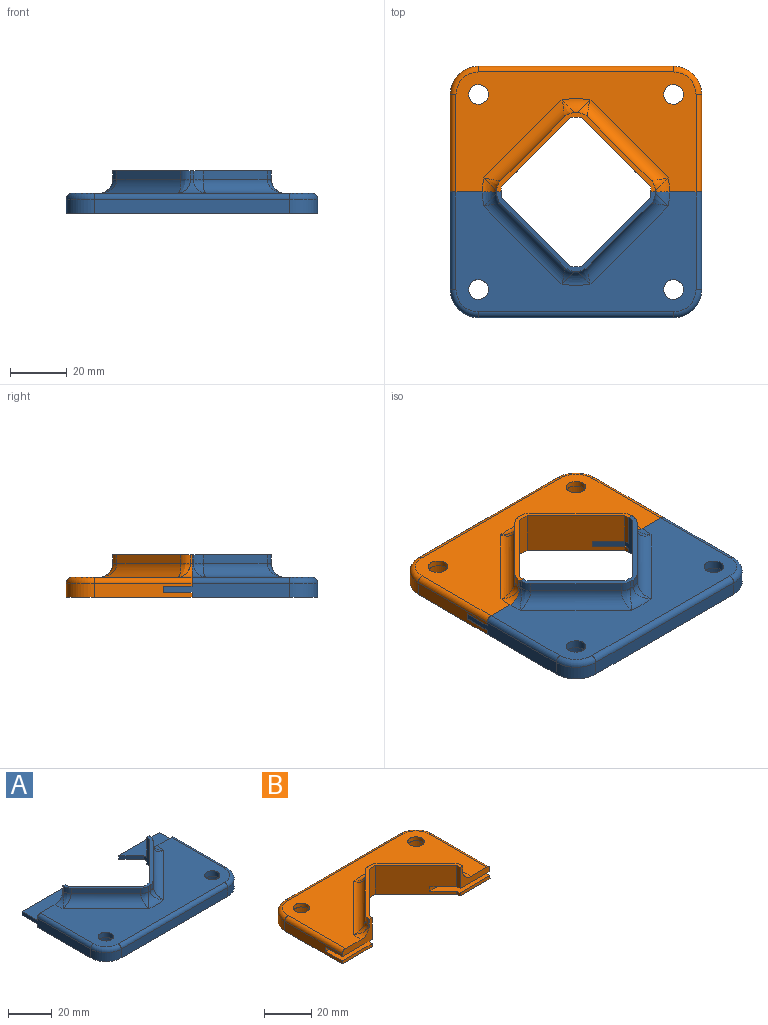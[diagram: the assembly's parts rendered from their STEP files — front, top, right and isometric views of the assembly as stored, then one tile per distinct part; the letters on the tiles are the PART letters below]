
ASSEMBLY  parts=2 mates=1
PART A: 54 faces, bbox 90.5x55.3x15.6 mm
  f0: plane 44.5x5mm, normal (1,0,0), area 192.5mm2, adj f2,f9,f35,f44,f45,f46,f47,f48
  f1: plane 44.5x5mm, normal (-1,0,0), area 192.5mm2, adj f2,f7,f31,f49,f50,f51,f52,f53
  f2: plane 88.9x44.45mm, normal (0,0,-1), area 2850.6mm2, adj f0,f1,f3,f4,f5,f6,f7,f8
  f3: cylinder r=26.44mm len=15mm, axis (0,0,-1), area 32.6mm2, adj f2,f20,f21,f25,f50,f51,f52,f53
  f4: cylinder r=26.44mm len=15mm, axis (0,0,-1), area 32.6mm2, adj f2,f22,f23,f25,f44,f45,f46,f47
  f5: cylinder r=6.5mm len=13mm, axis (0,0,-1), area 163.4mm2, adj f2,f14
  f6: cylinder r=6.5mm len=13mm, axis (0,0,-1), area 163.4mm2, adj f2,f12
  f7: cylinder r=9.95mm len=9.95mm, axis (0,0,-1), area 78.1mm2, adj f1,f2,f8,f32
  f8: plane 69x5mm, normal (0,-1,0), area 345mm2, adj f2,f7,f9,f33
  f9: cylinder r=9.95mm len=9.95mm, axis (0,0,-1), area 78.1mm2, adj f0,f2,f8,f34
  f10: plane 84.9x42.45mm, normal (0,0,1), area 2128.9mm2, adj f11,f13,f26,f27,f28,f29,f30,f31
  f11: cylinder r=3.5mm len=7mm, axis (0,0,-1), area 66mm2, adj f10,f12
  f12: plane 13x13mm, normal (0,0,-1), area 94.2mm2, adj f6,f11
  f13: cylinder r=3.5mm len=7mm, axis (0,0,-1), area 66mm2, adj f10,f14
  f14: plane 13x13mm, normal (0,0,-1), area 94.2mm2, adj f5,f13
  f15: plane 22.6x22.6mm, normal (0.71,-0.71,0), area 95.9mm2, adj f25,f27,f37,f41
  f16: cylinder r=28.04mm len=3mm, axis (0,0,-1), area 1.6mm2, adj f25,f29,f41,f46
  f17: cylinder r=28.04mm len=3mm, axis (0,0,-1), area 1.6mm2, adj f25,f30,f43,f51
  f18: plane 22.6x22.6mm, normal (-0.71,-0.71,0), area 95.9mm2, adj f25,f28,f39,f43
  f19: cylinder r=26.44mm len=15mm, axis (0,0,-1), area 57.5mm2, adj f2,f20,f23,f25
  f20: plane 24.46x24.46mm, normal (0.71,0.71,0), area 518.8mm2, adj f2,f3,f19,f25
  f21: plane 8.09x8.09mm, normal (0.71,-0.71,0), area 22.9mm2, adj f3,f49,f52,f53
  f22: plane 8.09x8.09mm, normal (-0.71,-0.71,0), area 22.9mm2, adj f4,f44,f47,f48
  f23: plane 24.46x24.46mm, normal (-0.71,0.71,0), area 518.8mm2, adj f2,f4,f19,f25
  f24: cylinder r=28.04mm len=3mm, axis (0,0,-1), area 3.2mm2, adj f25,f26,f37,f39
  f25: plane 56.08x28.04mm, normal (0,0,1), area 125.3mm2, adj f3,f4,f15,f16,f17,f18,f19,f20
  f26: torus R=33.04mm, axis (0,0,1), area 34.8mm2, adj f10,f24,f36,f38
  f27: cylinder r=5mm len=31.25mm, axis (0.71,0.71,0), area 272.4mm2, adj f10,f15,f36,f40
  f28: cylinder r=5mm len=31.25mm, axis (0.71,-0.71,0), area 272.4mm2, adj f10,f18,f38,f42
  f29: torus R=33.04mm, axis (0,0,1), area 17.4mm2, adj f10,f16,f40,f46
  f30: torus R=33.04mm, axis (0,0,1), area 17.4mm2, adj f10,f17,f42,f51
  f31: cylinder r=2mm len=34.5mm, axis (0,1,0), area 108.4mm2, adj f1,f10,f32,f51
  f32: torus R=7.95mm, axis (0,0,1), area 45.5mm2, adj f7,f10,f31,f33
  f33: cylinder r=2mm len=69mm, axis (-1,0,0), area 216.8mm2, adj f8,f10,f32,f34
  f34: torus R=7.95mm, axis (0,0,1), area 45.5mm2, adj f9,f10,f33,f35
  f35: cylinder r=2mm len=34.5mm, axis (0,-1,0), area 108.4mm2, adj f0,f10,f34,f46
  f36: bspline ~6.1x5.89mm, area 18.9mm2, adj f26,f27,f37
  f37: cylinder r=5mm len=3.44mm, axis (0,0,-1), area 11.5mm2, adj f15,f24,f25,f36
  f38: bspline ~6.1x5.89mm, area 18.9mm2, adj f26,f28,f39
  f39: cylinder r=5mm len=3.44mm, axis (0,0,-1), area 11.5mm2, adj f18,f24,f25,f38
  f40: bspline ~6.1x5.89mm, area 18.9mm2, adj f27,f29,f41
  f41: cylinder r=5mm len=3.44mm, axis (0,0,-1), area 11.5mm2, adj f15,f16,f25,f40
  f42: bspline ~6.1x5.89mm, area 18.9mm2, adj f28,f30,f43
  f43: cylinder r=5mm len=3.44mm, axis (0,0,-1), area 11.5mm2, adj f17,f18,f25,f42
  f44: plane 26.17x10mm, normal (0,0,-1), area 213.4mm2, adj f0,f4,f22,f45,f48
  f45: plane 18.01x1.8mm, normal (0,1,0), area 32.4mm2, adj f0,f2,f4,f44
  f46: plane 18.01x11.2mm, normal (0,1,0), area 74.9mm2, adj f0,f4,f10,f16,f25,f29,f35,f47
  f47: plane 26.17x10mm, normal (0,0,1), area 213.4mm2, adj f0,f4,f22,f46,f48
  f48: plane 26.17x2mm, normal (0,1,0), area 52.3mm2, adj f0,f22,f44,f47
  f49: plane 26.17x2mm, normal (0,1,0), area 52.3mm2, adj f1,f21,f52,f53
  f50: plane 18.01x1.8mm, normal (0,1,0), area 32.4mm2, adj f1,f2,f3,f52
  f51: plane 18.01x11.2mm, normal (0,1,0), area 74.9mm2, adj f1,f3,f10,f17,f25,f30,f31,f53
  f52: plane 26.17x10mm, normal (0,0,-1), area 213.4mm2, adj f1,f3,f21,f49,f50
  f53: plane 26.17x10mm, normal (0,0,1), area 213.4mm2, adj f1,f3,f21,f49,f51
PART B: 54 faces, bbox 90.5x45.3x15.6 mm
  f0: plane 34.5x5mm, normal (1,0,0), area 150mm2, adj f3,f14,f17,f44,f45,f46,f47,f48
  f1: plane 34.5x5mm, normal (-1,0,0), area 150mm2, adj f3,f13,f19,f49,f50,f51,f52,f53
  f2: plane 84.9x42.45mm, normal (0,0,1), area 2128.9mm2, adj f11,f12,f13,f14,f20,f22,f30,f31
  f3: plane 88.9x44.45mm, normal (0,0,-1), area 2850.6mm2, adj f0,f1,f7,f8,f15,f16,f17,f18
  f4: cylinder r=28.04mm len=3mm, axis (0,0,-1), area 1.6mm2, adj f10,f11,f37,f46
  f5: cylinder r=28.04mm len=3mm, axis (0,0,-1), area 1.6mm2, adj f10,f12,f39,f51
  f6: cylinder r=26.44mm len=11.15mm, axis (0,0,-1), area 21.4mm2, adj f7,f10,f51,f52
  f7: plane 24.46x24.46mm, normal (0.71,-0.71,0), area 493.1mm2, adj f3,f6,f10,f27,f28,f49,f52,f53
  f8: plane 24.46x24.46mm, normal (-0.71,-0.71,0), area 493.1mm2, adj f3,f9,f10,f28,f29,f45,f47,f48
  f9: cylinder r=26.44mm len=11.15mm, axis (0,0,-1), area 21.4mm2, adj f8,f10,f46,f47
  f10: plane 56.08x28.04mm, normal (0,0,1), area 125.3mm2, adj f4,f5,f6,f7,f8,f9,f24,f25
  f11: torus R=33.04mm, axis (0,0,1), area 17.4mm2, adj f2,f4,f36,f46
  f12: torus R=33.04mm, axis (0,0,1), area 17.4mm2, adj f2,f5,f38,f51
  f13: cylinder r=2mm len=34.5mm, axis (0,1,0), area 108.4mm2, adj f1,f2,f33,f51
  f14: cylinder r=2mm len=34.5mm, axis (0,-1,0), area 108.4mm2, adj f0,f2,f35,f46
  f15: cylinder r=6.5mm len=13mm, axis (0,0,-1), area 204.2mm2, adj f3,f23
  f16: cylinder r=6.5mm len=13mm, axis (0,0,-1), area 204.2mm2, adj f3,f21
  f17: cylinder r=9.95mm len=9.95mm, axis (0,0,-1), area 78.1mm2, adj f0,f3,f18,f35
  f18: plane 69x5mm, normal (0,1,0), area 345mm2, adj f3,f17,f19,f34
  f19: cylinder r=9.95mm len=9.95mm, axis (0,0,-1), area 78.1mm2, adj f1,f3,f18,f33
  f20: cylinder r=3.5mm len=7mm, axis (0,0,-1), area 44mm2, adj f2,f21
  f21: plane 13x13mm, normal (0,0,-1), area 94.2mm2, adj f16,f20
  f22: cylinder r=3.5mm len=7mm, axis (0,0,-1), area 44mm2, adj f2,f23
  f23: plane 13x13mm, normal (0,0,-1), area 94.2mm2, adj f15,f22
  f24: plane 22.6x22.6mm, normal (0.71,0.71,0), area 95.9mm2, adj f10,f30,f37,f41
  f25: cylinder r=28.04mm len=3mm, axis (0,0,-1), area 3.2mm2, adj f10,f32,f41,f43
  f26: plane 22.6x22.6mm, normal (-0.71,0.71,0), area 95.9mm2, adj f10,f31,f39,f43
  f27: cylinder r=26.44mm len=1.91mm, axis (0,0,-1), area 3.1mm2, adj f3,f7,f50,f53
  f28: cylinder r=26.44mm len=15mm, axis (0,0,-1), area 57.5mm2, adj f3,f7,f8,f10
  f29: cylinder r=26.44mm len=1.91mm, axis (0,0,-1), area 3.1mm2, adj f3,f8,f44,f45
  f30: cylinder r=5mm len=31.25mm, axis (-0.71,0.71,0), area 272.4mm2, adj f2,f24,f36,f40
  f31: cylinder r=5mm len=31.25mm, axis (-0.71,-0.71,0), area 272.4mm2, adj f2,f26,f38,f42
  f32: torus R=33.04mm, axis (0,0,1), area 34.8mm2, adj f2,f25,f40,f42
  f33: torus R=7.95mm, axis (0,0,1), area 45.5mm2, adj f2,f13,f19,f34
  f34: cylinder r=2mm len=69mm, axis (1,0,0), area 216.8mm2, adj f2,f18,f33,f35
  f35: torus R=7.95mm, axis (0,0,1), area 45.5mm2, adj f2,f14,f17,f34
  f36: bspline ~6.1x5.89mm, area 18.9mm2, adj f11,f30,f37
  f37: cylinder r=5mm len=3.44mm, axis (0,0,-1), area 11.5mm2, adj f4,f10,f24,f36
  f38: bspline ~6.1x5.89mm, area 18.9mm2, adj f12,f31,f39
  f39: cylinder r=5mm len=3.44mm, axis (0,0,-1), area 11.5mm2, adj f5,f10,f26,f38
  f40: bspline ~6.1x5.89mm, area 18.9mm2, adj f30,f32,f41
  f41: cylinder r=5mm len=3.44mm, axis (0,0,-1), area 11.5mm2, adj f10,f24,f25,f40
  f42: bspline ~6.1x5.89mm, area 18.9mm2, adj f31,f32,f43
  f43: cylinder r=5mm len=3.44mm, axis (0,0,-1), area 11.5mm2, adj f10,f25,f26,f42
  f44: plane 18.01x1.6mm, normal (0,-1,0), area 28.8mm2, adj f0,f3,f29,f45
  f45: plane 26.17x10mm, normal (0,0,1), area 213.4mm2, adj f0,f8,f29,f44,f48
  f46: plane 18.01x11.15mm, normal (0,-1,0), area 74mm2, adj f0,f2,f4,f9,f10,f11,f14,f47
  f47: plane 26.17x10mm, normal (0,0,-1), area 213.4mm2, adj f0,f8,f9,f46,f48
  f48: plane 26.17x2.25mm, normal (0,-1,0), area 58.9mm2, adj f0,f8,f45,f47
  f49: plane 26.17x2.25mm, normal (0,-1,0), area 58.9mm2, adj f1,f7,f52,f53
  f50: plane 18.01x1.6mm, normal (0,-1,0), area 28.8mm2, adj f1,f3,f27,f53
  f51: plane 18.01x11.15mm, normal (0,-1,0), area 74mm2, adj f1,f2,f5,f6,f10,f12,f13,f52
  f52: plane 26.17x10mm, normal (0,0,-1), area 213.4mm2, adj f1,f6,f7,f49,f51
  f53: plane 26.17x10mm, normal (0,0,1), area 213.4mm2, adj f1,f7,f27,f49,f50
PLACE A t=(-12.08,49.02,-24.42)mm
PLACE B t=(-12.08,49.02,-24.42)mm
MATE fastened A.f51 <-> B.f51  axis (0,1,0) through (-40.12,49.02,-9.42)mm
